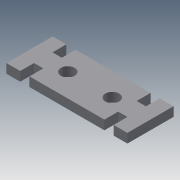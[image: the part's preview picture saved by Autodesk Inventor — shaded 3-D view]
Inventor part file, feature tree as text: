
AUTODESK INVENTOR PART (.ipt)
format: ipt  version: 2013 (Build 170138000, 138)  size: 115,200 bytes
history: native  units: mm
features: extrude x3, sketch x3
ambient origin geometry x8: Origin, YZ Plane, XZ Plane, XY Plane, X Axis, Y Axis, Z Axis, Center Point
bodies: Solid1 (feature_tree)
feature tree (6):
  extrude  "Extrusion1"  Depth=50.0mm
  sketch  "Sketch2"  dims[d2=24.1mm d3=24.1mm]
  extrude  "Extrusion2"  Depth=24.1mm
  extrude  "Extrusion3"  Depth=15.0mm
  sketch  "Sketch1"  dims[d0=131.0mm d1=50.0mm]
  sketch  "Sketch3"  dims[d4=15.0mm d5=15.0mm d6=10.0mm d7=0.0mm d10=15.0mm d12=15.0mm d14=15.0mm d16=15.0mm d18=10.0mm d19=0.0mm d20=10.0mm d21=0.0mm]
